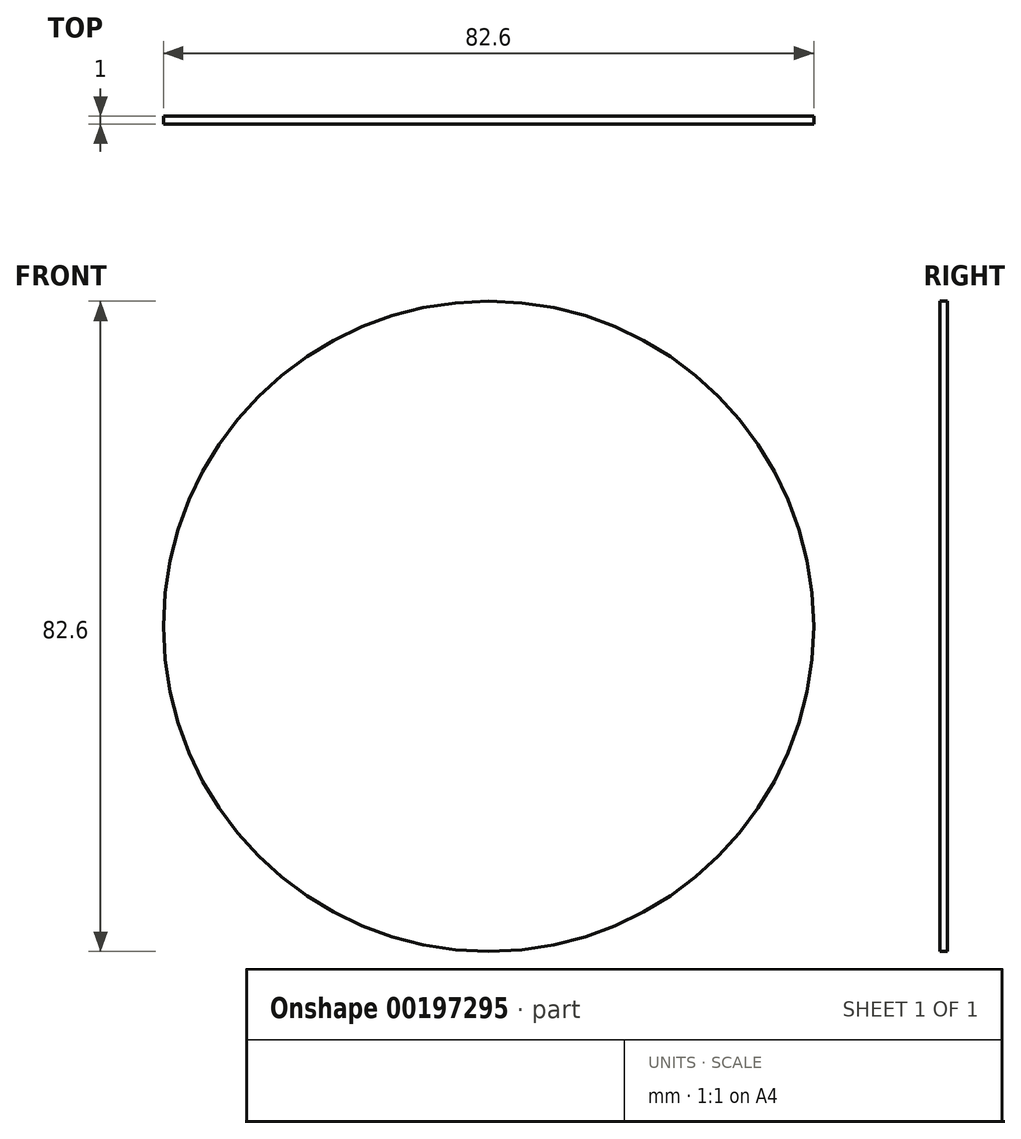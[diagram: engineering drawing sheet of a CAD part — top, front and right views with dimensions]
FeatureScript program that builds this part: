
annotation { "Feature Type Name" : "Feature", "Feature Type Description" : "" }
export const myFeature = defineFeature(function(context is Context, id is Id, definition is map)
    precondition{}
    {
        {
            var Q0;
            Q0=qCreatedBy(makeId("Front.planeOp"),FACE);
            var sketch = newSketch(context, id + "F0", { "sketchPlane" : qUnion([Q0])});
            skCircle(sketch, "E0", {"center": v(0, 0) * mm, "radius": 28.6 * mm});
            skCircle(sketch, "E1", {"center": v(0, 0) * mm, "radius": 8.3 * mm});
            skCircle(sketch, "E2.0", {"center": v(0, 0) * mm, "radius": 41.3 * mm});
            skSolve(sketch);
        }
        {
            var Q0;
            Q0=makeQuery(id+"F0.imprint","IMPRINT",FACE,{"disambiguationData":[TD([[makeQuery(id+"F0.imprint","IMPRINT",EDGE,{"derivedFrom":sQuery(id+"F0.wireOp",EDGE,"E1")}),1.0]])]});
            var Q1;
            Q1=makeQuery(id+"F0.imprint","IMPRINT",FACE,{"disambiguationData":[TD([[makeQuery(id+"F0.imprint","IMPRINT",EDGE,{"derivedFrom":sQuery(id+"F0.wireOp",EDGE,"E0")}),-1.0]])]});
            var Q2;
            Q2=makeQuery(id+"F0.imprint","IMPRINT",FACE,{"disambiguationData":[TD([[makeQuery(id+"F0.imprint","IMPRINT",EDGE,{"derivedFrom":sQuery(id+"F0.wireOp",EDGE,"E0")}),1.0]])]});
            extrude(context, id + "F1", {"entities" : qUnion([Q0, Q1, Q2]), "depth" : mm});
        }
    });
